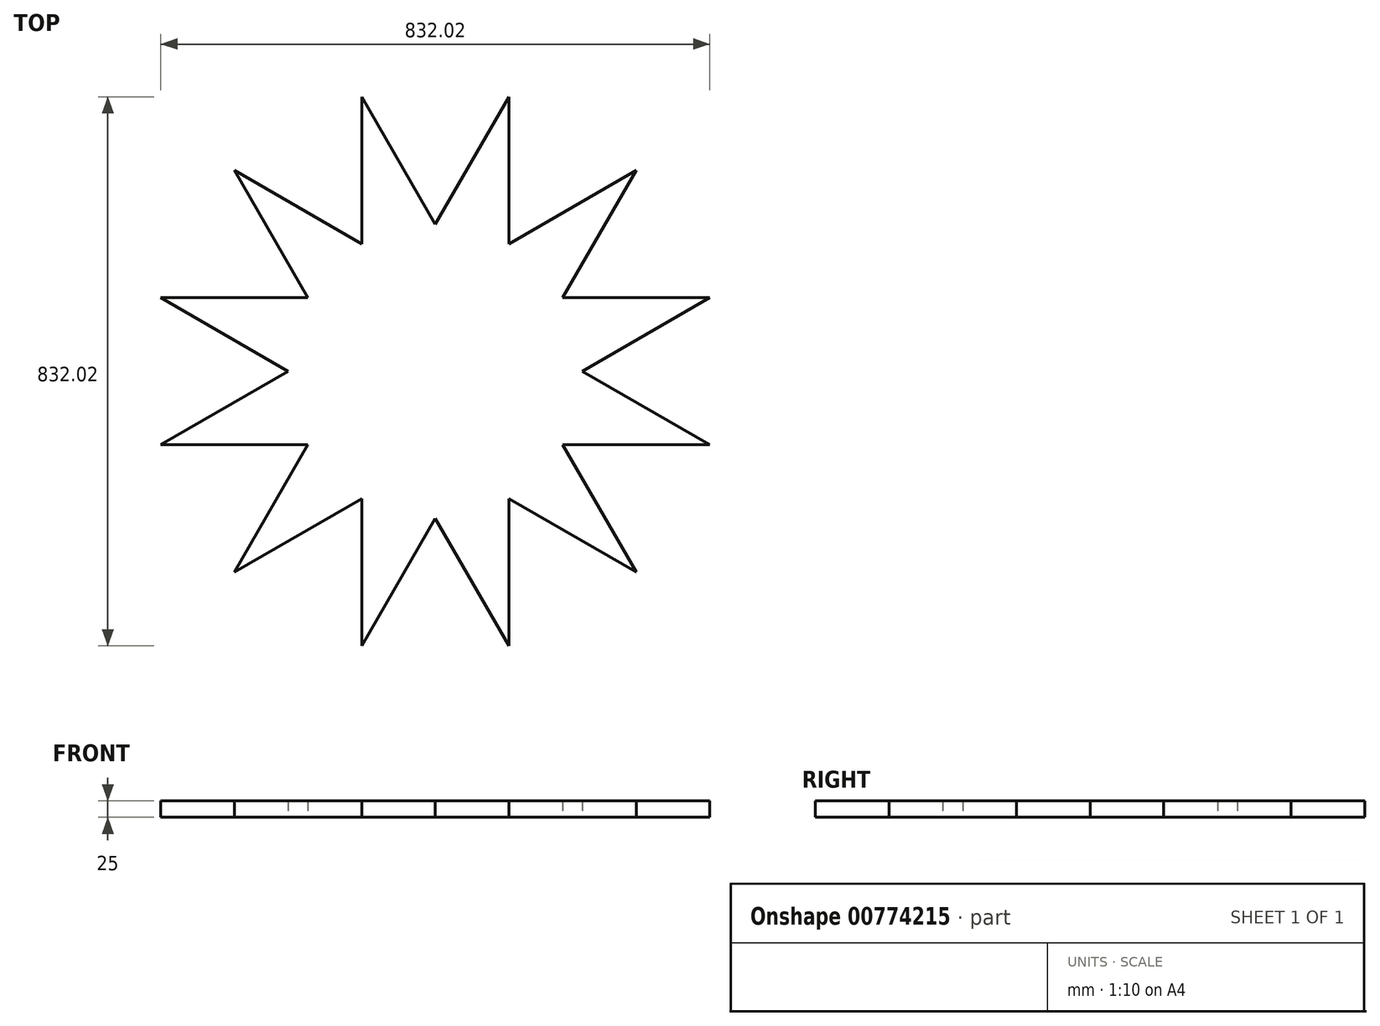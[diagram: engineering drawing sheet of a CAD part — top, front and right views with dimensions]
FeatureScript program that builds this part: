
annotation { "Feature Type Name" : "Feature", "Feature Type Description" : "" }
export const myFeature = defineFeature(function(context is Context, id is Id, definition is map)
    precondition{}
    {
        {
            var Q0;
            Q0=qCreatedBy(makeId("Top.planeOp"),FACE);
            var sketch = newSketch(context, id + "F0", { "sketchPlane" : qUnion([Q0])});
            skCircle(sketch, "E0", {"center": v(0, 0) * mm, "radius": 700 * mm});
            skCircle(sketch, "E1", {"center": v(0, 0) * mm, "radius": 900 * mm});
            skLineSegment(sketch, "E2", {"start": v(-350, 606.22) * mm, "end": v(-350, 829.16) * mm, "construction": true});
            skLineSegment(sketch, "E3", {"start": v(350, 606.22) * mm, "end": v(350, 829.16) * mm, "construction": true});
            skLineSegment(sketch, "E4", {"start": v(-350, 829.16) * mm, "end": v(0, 222.94) * mm});
            skLineSegment(sketch, "E5", {"start": v(0, 222.94) * mm, "end": v(375.18, 872.78) * mm});
            skCircle(sketch, "E6", {"center": v(0, 0) * mm, "radius": 950 * mm});
            skLineSegment(sketch, "E7", {"start": v(-350, 829.16) * mm, "end": v(-375.18, 872.78) * mm});
            skLineSegment(sketch, "E8.1.0", {"start": v(-943.44, 111.47) * mm, "end": v(-193.07, 111.47) * mm});
            skLineSegment(sketch, "E8.1.1", {"start": v(-193.07, 111.47) * mm, "end": v(-568.25, 761.3) * mm});
            skLineSegment(sketch, "E8.2.0", {"start": v(-568.25, -761.3) * mm, "end": v(-193.07, -111.47) * mm});
            skLineSegment(sketch, "E8.2.1", {"start": v(-193.07, -111.47) * mm, "end": v(-943.44, -111.47) * mm});
            skLineSegment(sketch, "E8.3.0", {"start": v(375.18, -872.78) * mm, "end": v(0, -222.94) * mm});
            skLineSegment(sketch, "E8.3.1", {"start": v(0, -222.94) * mm, "end": v(-375.18, -872.78) * mm});
            skLineSegment(sketch, "E8.4.0", {"start": v(943.44, -111.47) * mm, "end": v(193.07, -111.47) * mm});
            skLineSegment(sketch, "E8.4.1", {"start": v(193.07, -111.47) * mm, "end": v(568.25, -761.3) * mm});
            skLineSegment(sketch, "E8.5.0", {"start": v(568.25, 761.3) * mm, "end": v(193.07, 111.47) * mm});
            skLineSegment(sketch, "E8.5.1", {"start": v(193.07, 111.47) * mm, "end": v(943.44, 111.47) * mm});
            skPoint(sketch, "E9.orphan", {"position": v(-893.07, 111.47) * mm});
            skPoint(sketch, "E10.orphan", {"position": v(-543.07, -717.69) * mm});
            skPoint(sketch, "E11.orphan", {"position": v(350, -829.16) * mm});
            skPoint(sketch, "E12.orphan", {"position": v(893.07, -111.47) * mm});
            skPoint(sketch, "E13.orphan", {"position": v(543.07, 717.69) * mm});
            skCircle(sketch, "E14", {"center": v(0, 0) * mm, "radius": 222.94 * mm, "construction": true});
            skLineSegment(sketch, "E15", {"start": v(-193.07, 111.47) * mm, "end": v(0, 222.94) * mm, "construction": true});
            skLineSegment(sketch, "E16", {"start": v(-568.25, 761.3) * mm, "end": v(-375.18, 872.78) * mm, "construction": true});
            skLineSegment(sketch, "E17", {"start": v(-96.54, 167.2) * mm, "end": v(-475, 822.72) * mm, "construction": true});
            skLineSegment(sketch, "E18", {"start": v(-111.47, 193.07) * mm, "end": v(-304.54, 304.54) * mm});
            skLineSegment(sketch, "E19", {"start": v(-111.47, 193.07) * mm, "end": v(-111.47, 416) * mm});
            skLineSegment(sketch, "E20", {"start": v(-111.47, 193.07) * mm, "end": v(-208, 137.34) * mm, "construction": true});
            skLineSegment(sketch, "E21.1.0", {"start": v(-222.94, 0) * mm, "end": v(-416, -111.47) * mm});
            skLineSegment(sketch, "E21.1.1", {"start": v(-222.94, 0) * mm, "end": v(-416, 111.47) * mm});
            skLineSegment(sketch, "E21.2.0", {"start": v(-111.47, -193.07) * mm, "end": v(-111.47, -416) * mm});
            skLineSegment(sketch, "E21.2.1", {"start": v(-111.47, -193.07) * mm, "end": v(-304.54, -304.54) * mm});
            skLineSegment(sketch, "E21.3.0", {"start": v(111.47, -193.07) * mm, "end": v(304.54, -304.54) * mm});
            skLineSegment(sketch, "E21.3.1", {"start": v(111.47, -193.07) * mm, "end": v(111.47, -416) * mm});
            skLineSegment(sketch, "E21.4.0", {"start": v(222.94, 0) * mm, "end": v(416, 111.47) * mm});
            skLineSegment(sketch, "E21.4.1", {"start": v(222.94, 0) * mm, "end": v(416, -111.47) * mm});
            skLineSegment(sketch, "E21.5.0", {"start": v(111.47, 193.07) * mm, "end": v(111.47, 416) * mm});
            skLineSegment(sketch, "E21.5.1", {"start": v(111.47, 193.07) * mm, "end": v(304.54, 304.54) * mm});
            skSolve(sketch);
        }
        {
            var Q0;
            {var subQ6=sQuery(id+"F0.wireOp",EDGE,"E18");Q0=makeQuery(id+"F0.imprint","IMPRINT",FACE,{"disambiguationData":[TD([[makeQuery(id+"F0.imprint","IMPRINT",EDGE,{"derivedFrom":subQ6}),1.0]])]});}
            extrude(context, id + "F1", {"entities" : qUnion([Q0]), "depth" : 25 * mm, "offsetDistance" : 25 * mm});
        }
    });
